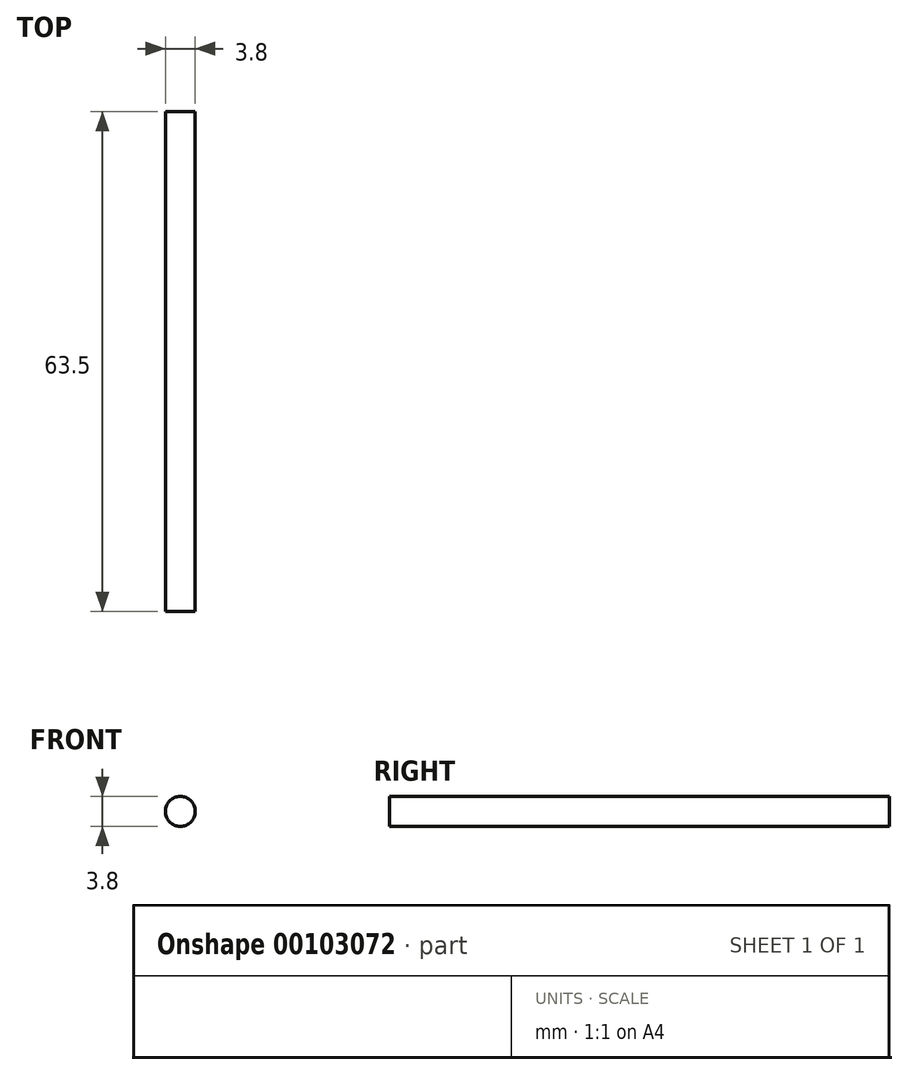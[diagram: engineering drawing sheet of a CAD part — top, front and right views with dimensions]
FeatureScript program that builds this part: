
annotation { "Feature Type Name" : "Feature", "Feature Type Description" : "" }
export const myFeature = defineFeature(function(context is Context, id is Id, definition is map)
    precondition{}
    {
        {
            var Q0;
            Q0=qCreatedBy(makeId("Top.planeOp"),FACE);
            var sketch = newSketch(context, id + "F0", { "sketchPlane" : qUnion([Q0])});
            skLineSegment(sketch, "E0", {"start": v(-11.51, 72.58) * mm, "end": v(-11.51, 9.08) * mm});
            skLineSegment(sketch, "E1", {"start": v(-9.61, 72.58) * mm, "end": v(-9.61, 37.16) * mm});
            skLineSegment(sketch, "E2", {"start": v(-9.61, 37.16) * mm, "end": v(-9.61, 9.08) * mm});
            skLineSegment(sketch, "E3", {"start": v(-11.51, 72.58) * mm, "end": v(-9.61, 72.58) * mm});
            skLineSegment(sketch, "E4", {"start": v(-11.51, 37.16) * mm, "end": v(-9.61, 37.16) * mm});
            skLineSegment(sketch, "E5", {"start": v(-11.51, 9.08) * mm, "end": v(-9.61, 9.08) * mm});
            skSolve(sketch);
        }
        {
            var Q0;
            Q0=qSketchRegion(id+"F0",true);
            var Q1;
            Q1=qConstructionFilter(qBodyType(qCreatedBy(id+"F0",EDGE),BodyType.WIRE),ConstructionObject.NO);
            var Q2;
            Q2=sQuery(id+"F0.wireOp",EDGE,"E0");
            revolve(context, id + "F1", {"entities" : qUnion([Q0]), "surfaceEntities" : qUnion([Q1]), "axis" : qUnion([Q2]), "revolveType" : RevolveType.FULL});
        }
    });
